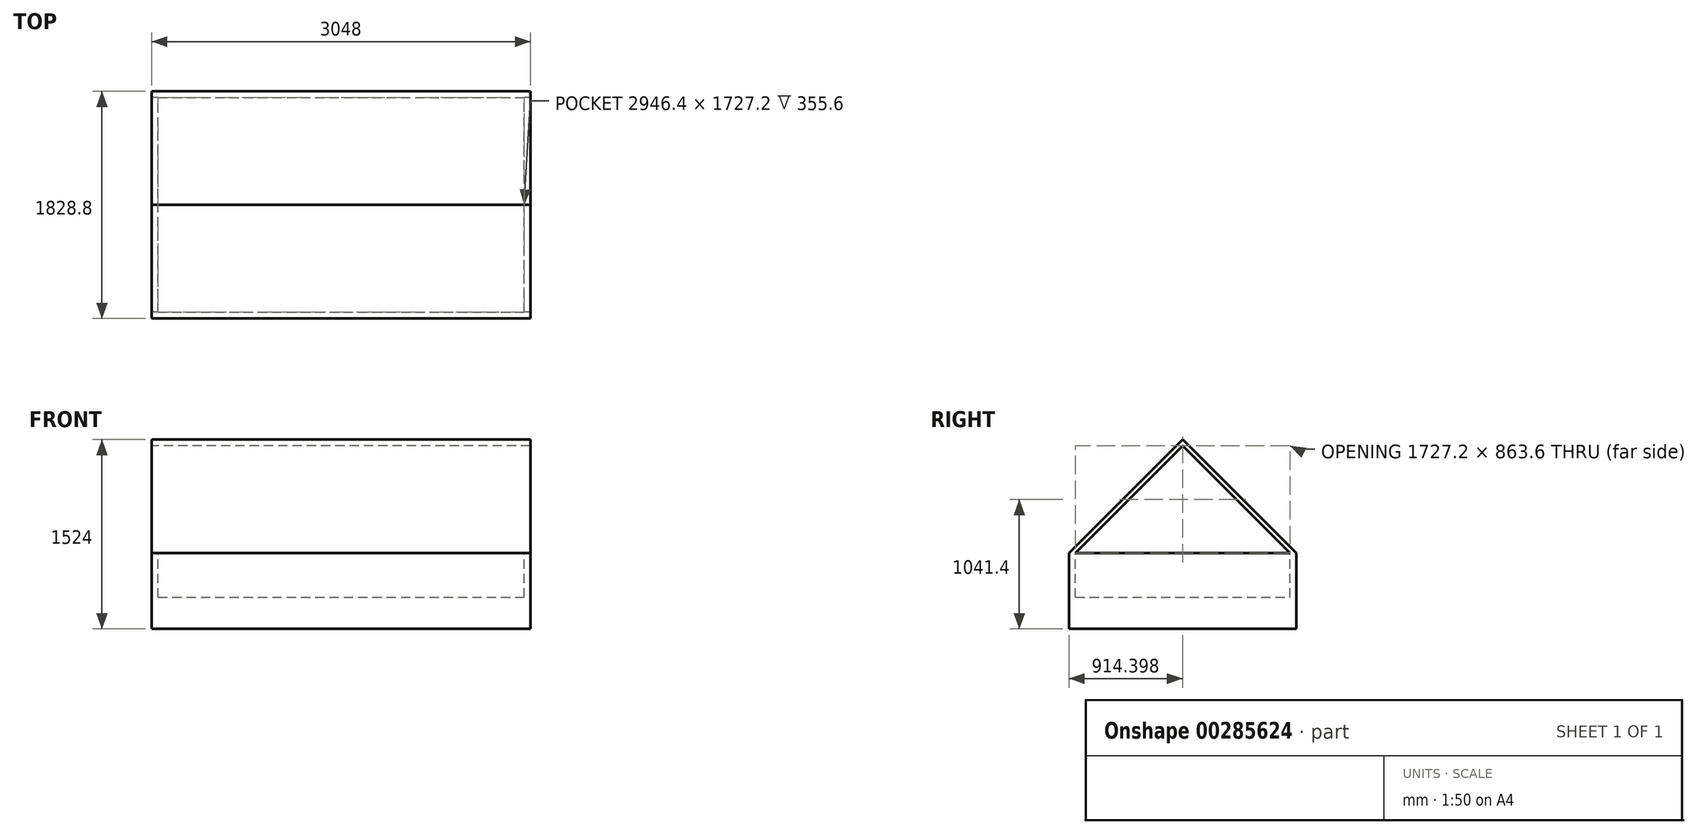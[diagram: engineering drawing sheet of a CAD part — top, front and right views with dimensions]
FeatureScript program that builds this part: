
annotation { "Feature Type Name" : "Feature", "Feature Type Description" : "" }
export const myFeature = defineFeature(function(context is Context, id is Id, definition is map)
    precondition{}
    {
        {
            var Q0;
            Q0=qCreatedBy(makeId("Top.planeOp"),FACE);
            var sketch = newSketch(context, id + "F0", { "sketchPlane" : qUnion([Q0])});
            skLineSegment(sketch, "E0.bottom", {"start": v(-1517.9, 472.29) * mm, "end": v(1530.1, 472.29) * mm});
            skLineSegment(sketch, "E0.top", {"start": v(-1517.9, -1356.51) * mm, "end": v(1530.1, -1356.51) * mm});
            skLineSegment(sketch, "E0.left", {"start": v(-1517.9, 472.29) * mm, "end": v(-1517.9, -1356.51) * mm});
            skLineSegment(sketch, "E0.right", {"start": v(1530.1, 472.29) * mm, "end": v(1530.1, -1356.51) * mm});
            skSolve(sketch);
        }
        {
            var Q0;
            Q0=makeQuery(id+"F0.imprint","IMPRINT",FACE,{"disambiguationData":[TD([[makeQuery(id+"F0.imprint","IMPRINT",EDGE,{"derivedFrom":sQuery(id+"F0.wireOp",EDGE,"E0.bottom")}),-1.0]])]});
            extrude(context, id + "F1", {"entities" : qUnion([Q0]), "depth" : 457.2 * mm});
        }
        {
            var Q0;
            Q0=makeQuery(id+"F1.opExtrude","CAP_FACE",FACE,{"disambiguationData":[OSD([sQuery(id+"F0.wireOp",EDGE,"E0.bottom"),sQuery(id+"F0.wireOp",EDGE,"E0.top"),sQuery(id+"F0.wireOp",EDGE,"E0.left"),sQuery(id+"F0.wireOp",EDGE,"E0.right")])],"isStart":false});
            var sketch = newSketch(context, id + "F2", { "sketchPlane" : qUnion([Q0])});
            skLineSegment(sketch, "E1.bottom", {"start": v(-1467.1, -1305.71) * mm, "end": v(1479.3, -1305.71) * mm});
            skLineSegment(sketch, "E1.top", {"start": v(-1467.1, 421.49) * mm, "end": v(1479.3, 421.49) * mm});
            skLineSegment(sketch, "E1.left", {"start": v(-1467.1, -1305.71) * mm, "end": v(-1467.1, 421.49) * mm});
            skLineSegment(sketch, "E1.right", {"start": v(1479.3, -1305.71) * mm, "end": v(1479.3, 421.49) * mm});
            skSolve(sketch);
        }
        {
            var Q0;
            Q0=makeQuery(id+"F2.imprint","IMPRINT",FACE,{"disambiguationData":[TD([[makeQuery(id+"F2.imprint","IMPRINT",EDGE,{"derivedFrom":sQuery(id+"F2.wireOp",EDGE,"E1.bottom")}),1.0]])]});
            extrude(context, id + "F3", {"entities" : qUnion([Q0]), "operationType" : NewBodyOperationType.REMOVE, "oppositeDirection" : true, "depth" : 355.6 * mm});
        }
        {
            var Q0;
            Q0=makeQuery(id+"F1.opExtrude","SWEPT_FACE",FACE,{"disambiguationData":[OSD([sQuery(id+"F0.wireOp",EDGE,"E0.left")])]});
            var sketch = newSketch(context, id + "F4", { "sketchPlane" : qUnion([Q0])});
            skLineSegment(sketch, "E2", {"start": v(-472.29, 457.2) * mm, "end": v(442.11, 1371.6) * mm});
            skPoint(sketch, "E2.endSnap0", {"position": v(442.11, 457.2) * mm});
            skLineSegment(sketch, "E3", {"start": v(1356.51, 457.2) * mm, "end": v(442.11, 1371.6) * mm});
            skSolve(sketch);
        }
        {
            var Q0;
            Q0=makeQuery(id+"F1.opExtrude","SWEPT_FACE",FACE,{"disambiguationData":[OSD([sQuery(id+"F0.wireOp",EDGE,"E0.right")])]});
            var sketch = newSketch(context, id + "F5", { "sketchPlane" : qUnion([Q0])});
            skLineSegment(sketch, "E4", {"start": v(-1356.51, 457.2) * mm, "end": v(-442.11, 1371.6) * mm});
            skLineSegment(sketch, "E5", {"start": v(472.29, 457.2) * mm, "end": v(-442.11, 1371.6) * mm});
            skSolve(sketch);
        }
        {
            var Q0;
            Q0=makeQuery(id+"F1.opExtrude","CAP_FACE",FACE,{"disambiguationData":[OSD([sQuery(id+"F0.wireOp",EDGE,"E0.bottom"),sQuery(id+"F0.wireOp",EDGE,"E0.top"),sQuery(id+"F0.wireOp",EDGE,"E0.left"),sQuery(id+"F0.wireOp",EDGE,"E0.right")])],"isStart":true});
            var sketch = newSketch(context, id + "F6", { "sketchPlane" : qUnion([Q0])});
            skLineSegment(sketch, "E6.bottom", {"start": v(-1517.9, -472.29) * mm, "end": v(1530.1, -472.29) * mm});
            skLineSegment(sketch, "E6.top", {"start": v(-1517.9, 1356.51) * mm, "end": v(1530.1, 1356.51) * mm});
            skLineSegment(sketch, "E6.left", {"start": v(-1517.9, -472.29) * mm, "end": v(-1517.9, 1356.51) * mm});
            skLineSegment(sketch, "E6.right", {"start": v(1530.1, -472.29) * mm, "end": v(1530.1, 1356.51) * mm});
            skSolve(sketch);
        }
        {
            var Q0;
            Q0=makeQuery(id+"F6.imprint","IMPRINT",FACE,{"disambiguationData":[TD([[makeQuery(id+"F6.imprint","IMPRINT",EDGE,{"derivedFrom":sQuery(id+"F6.wireOp",EDGE,"E6.bottom")}),1.0]])]});
            extrude(context, id + "F7", {"entities" : qUnion([Q0]), "operationType" : NewBodyOperationType.ADD, "depth" : 152.4 * mm});
        }
        {
            var Q0;
            Q0=makeQuery(id+"F5.imprint","IMPRINT",FACE,{"disambiguationData":[TD([[makeQuery(id+"F5.imprint","IMPRINT",EDGE,{"derivedFrom":sQuery(id+"F5.wireOp",EDGE,"E4")}),-1.0]])]});
            extrude(context, id + "F8", {"entities" : qUnion([Q0]), "operationType" : NewBodyOperationType.ADD, "oppositeDirection" : true, "depth" : 3048 * mm});
        }
        {
            var Q0;
            Q0=makeQuery(id+"F4.imprint","IMPRINT",FACE,{"disambiguationData":[TD([[makeQuery(id+"F4.imprint","IMPRINT",EDGE,{"derivedFrom":sQuery(id+"F4.wireOp",EDGE,"E2")}),-1.0]])]});
            var sketch = newSketch(context, id + "F9", { "sketchPlane" : qUnion([Q0])});
            skLineSegment(sketch, "E7", {"start": v(-421.49, 457.2) * mm, "end": v(1305.71, 457.2) * mm});
            skLineSegment(sketch, "E8", {"start": v(1305.71, 457.2) * mm, "end": v(442.11, 1320.8) * mm});
            skPoint(sketch, "E8.endSnap0", {"position": v(442.11, 457.2) * mm});
            skLineSegment(sketch, "E9", {"start": v(442.11, 1320.8) * mm, "end": v(-421.49, 457.2) * mm});
            skSolve(sketch);
        }
        {
            var Q0;
            Q0=makeQuery(id+"F9.imprint","IMPRINT",FACE,{"disambiguationData":[TD([[makeQuery(id+"F9.imprint","IMPRINT",EDGE,{"derivedFrom":sQuery(id+"F9.wireOp",EDGE,"E7")}),1.0]])]});
            extrude(context, id + "F10", {"entities" : qUnion([Q0]), "operationType" : NewBodyOperationType.REMOVE, "oppositeDirection" : true, "depth" : 3048 * mm});
        }
    });
